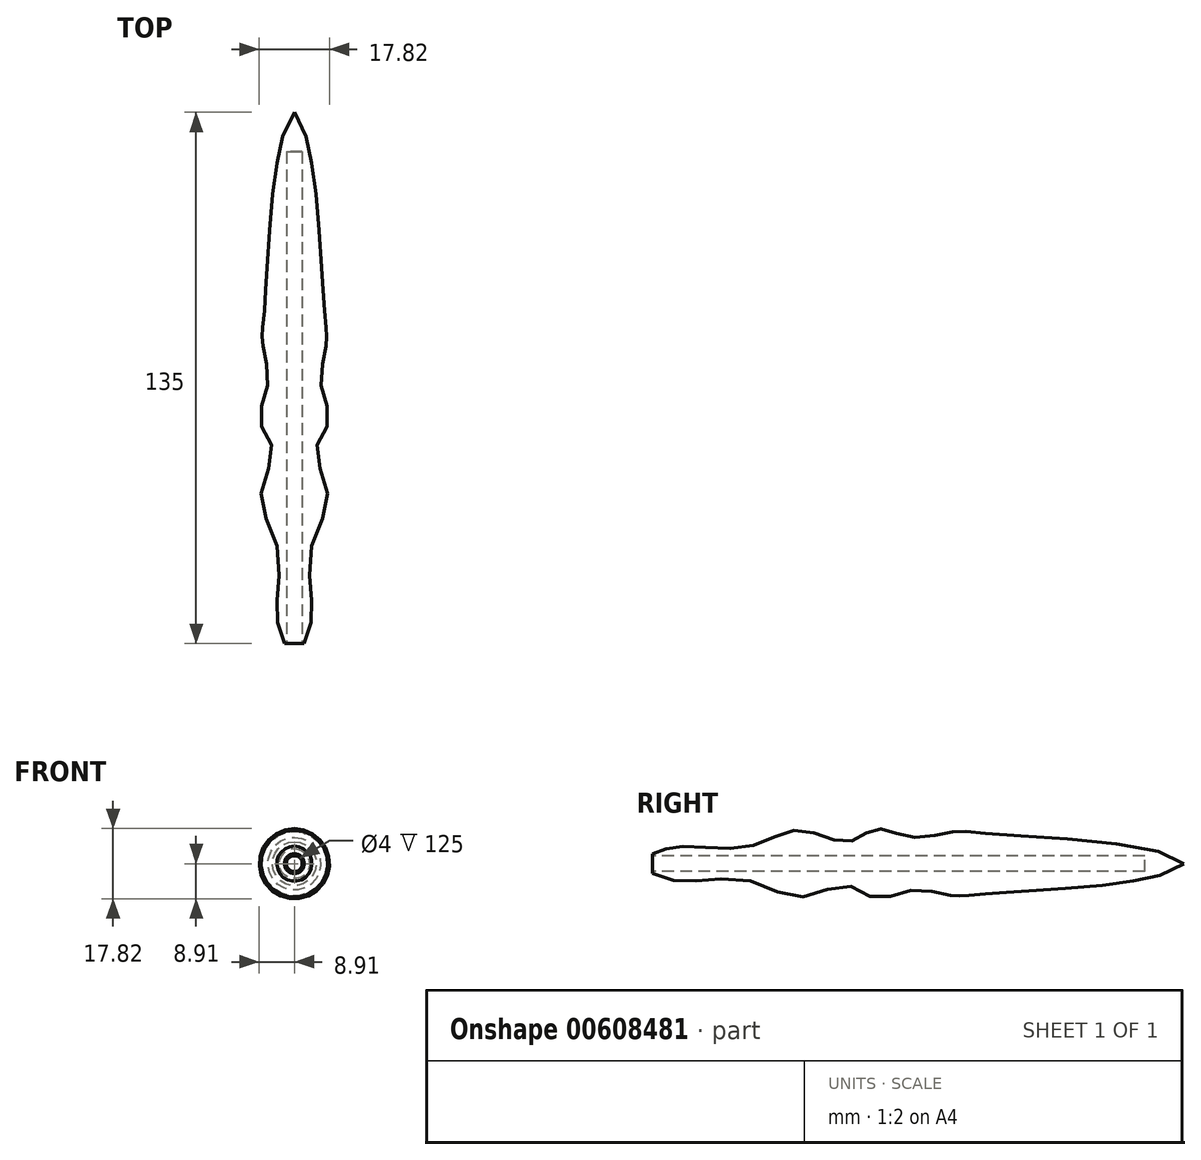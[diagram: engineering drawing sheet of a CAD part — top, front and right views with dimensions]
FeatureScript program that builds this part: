
annotation { "Feature Type Name" : "Feature", "Feature Type Description" : "" }
export const myFeature = defineFeature(function(context is Context, id is Id, definition is map)
    precondition{}
    {
        {
            var Q0;
            Q0=qCreatedBy(makeId("Right.planeOp"),FACE);
            var sketch = newSketch(context, id + "F0", { "sketchPlane" : qUnion([Q0])});
            skLineSegment(sketch, "E0", {"start": v(0, 0) * mm, "end": v(135, 0) * mm});
            skLineSegment(sketch, "E1", {"start": v(0, 0) * mm, "end": v(0, 2.5) * mm});
            skFitSpline(sketch, "E2", {"points": [v(0, 2.5) * mm, v(7.14, 4.42) * mm, v(23.94, 4.24) * mm, v(37.43, 8.49) * mm, v(49.46, 5.6) * mm, v(56.82, 8.86) * mm, v(65.32, 6.83) * mm, v(76.22, 8.09) * mm, v(85.27, 7.56) * mm, v(135, 0) * mm], "startDerivative": vector(68.83, 30.54) * mm, "endDerivative": vector(84.36, -84.66) * mm});
            skSolve(sketch);
        }
        {
            var Q0;
            Q0=makeQuery(id+"F0.imprint","IMPRINT",FACE,{"disambiguationData":[TD([[makeQuery(id+"F0.imprint","IMPRINT",EDGE,{"derivedFrom":sQuery(id+"F0.wireOp",EDGE,"E0")}),1.0]])]});
            var Q1;
            Q1=sQuery(id+"F0.wireOp",EDGE,"E0");
            revolve(context, id + "F1", {"entities" : qUnion([Q0]), "axis" : qUnion([Q1]), "revolveType" : RevolveType.FULL});
        }
        {
            var Q0;
            Q0=makeQuery(id+"F1.opRevolve","SWEPT_FACE",FACE,{"disambiguationData":[OSD([sQuery(id+"F0.wireOp",EDGE,"E1")])]});
            var sketch = newSketch(context, id + "F2", { "sketchPlane" : qUnion([Q0])});
            skCircle(sketch, "E3", {"center": v(0, 0) * mm, "radius": 2 * mm});
            skSolve(sketch);
        }
        {
            var Q0;
            Q0=makeQuery(id+"F2.imprint","IMPRINT",FACE,{"disambiguationData":[TD([[makeQuery(id+"F2.imprint","IMPRINT",EDGE,{"derivedFrom":sQuery(id+"F2.wireOp",EDGE,"E3")}),1.0]])]});
            extrude(context, id + "F3", {"entities" : qUnion([Q0]), "operationType" : NewBodyOperationType.REMOVE, "oppositeDirection" : true, "depth" : 125 * mm, "offsetDistance" : 25 * mm});
        }
    });
